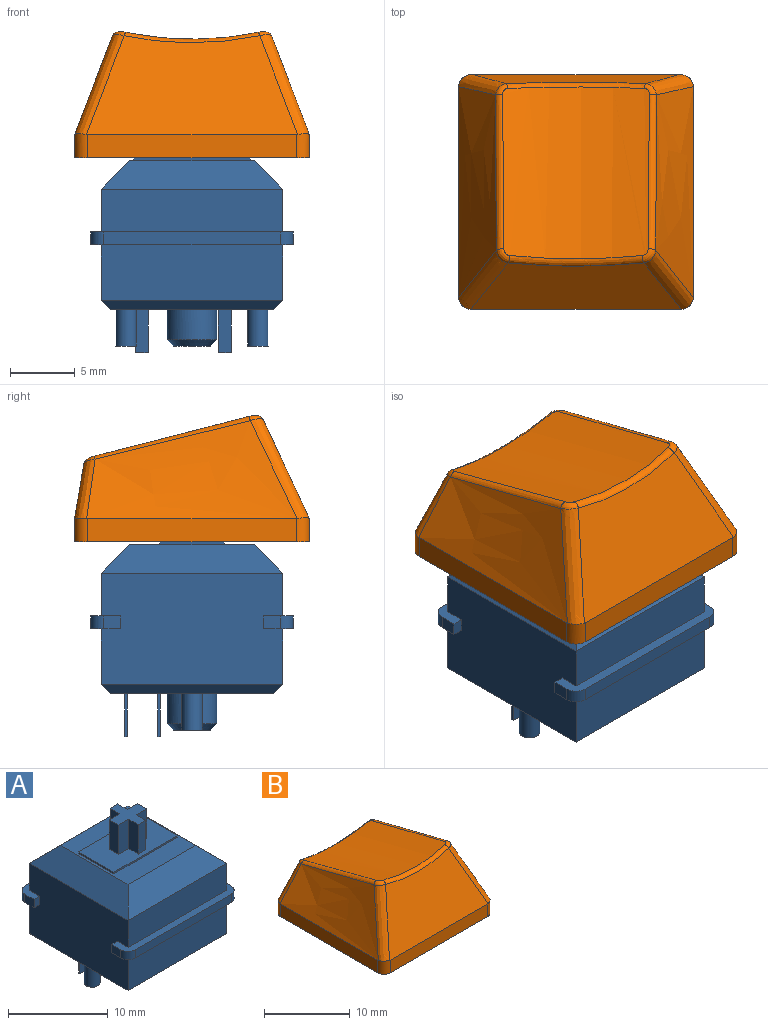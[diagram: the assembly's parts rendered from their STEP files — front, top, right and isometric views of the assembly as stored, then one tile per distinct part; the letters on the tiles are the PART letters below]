
ASSEMBLY  parts=2 mates=1
PART A: 69 faces, bbox 15.6x15.6x18.6 mm
  f0: plane 15.6x2.3mm, normal (0,0,-1), area 14.4mm2, adj f2,f3,f28,f30,f35,f60,f62,f63
  f1: plane 15.6x2.3mm, normal (0,0,-1), area 14.4mm2, adj f28,f30,f33,f34,f36,f59,f61,f64
  f2: plane 1.3x1mm, normal (1,0,0), area 1.3mm2, adj f0,f32,f62,f66
  f3: plane 1.3x1mm, normal (-1,0,0), area 1.3mm2, adj f0,f32,f63,f68
  f4: plane 15.6x2.3mm, normal (0,0,1), area 14.4mm2, adj f28,f30,f31,f33,f34,f36,f61,f64
  f5: plane 14x2.2mm, normal (-0.71,0,0.71), area 36.7mm2, adj f6,f7,f26,f30
  f6: plane 14x2.2mm, normal (0,-0.71,0.71), area 36.7mm2, adj f5,f7,f27,f31
  f7: plane 9.6x9.6mm, normal (0,0,1), area 47.2mm2, adj f5,f6,f8,f9,f10,f11,f26,f27
  f8: plane 5x0.2mm, normal (1,0,0), area 1mm2, adj f7,f9,f11,f12
  f9: plane 9x0.2mm, normal (0,1,0), area 1.8mm2, adj f7,f8,f10,f12
  f10: plane 5x0.2mm, normal (-1,0,0), area 1mm2, adj f7,f9,f11,f12
  f11: plane 9x0.2mm, normal (0,-1,0), area 1.8mm2, adj f7,f8,f10,f12
  f12: plane 9x5mm, normal (0,0,1), area 36.9mm2, adj f8,f9,f10,f11,f13,f14,f15,f16
  f13: plane 3.6x1.35mm, normal (1,0,0), area 4.9mm2, adj f12,f14,f24,f25
  f14: plane 3.6x1.08mm, normal (0,1,0), area 3.9mm2, adj f12,f13,f15,f25
  f15: plane 3.6x1.35mm, normal (-1,0,0), area 4.9mm2, adj f12,f14,f16,f25
  f16: plane 3.6x1.46mm, normal (0,1,0), area 5.3mm2, adj f12,f15,f17,f25
  f17: plane 3.6x1.3mm, normal (-1,0,0), area 4.7mm2, adj f12,f16,f18,f25
  f18: plane 3.6x1.46mm, normal (0,-1,0), area 5.3mm2, adj f12,f17,f19,f25
  f19: plane 3.6x1.35mm, normal (-1,0,0), area 4.9mm2, adj f12,f18,f20,f25
  f20: plane 3.6x1.08mm, normal (0,-1,0), area 3.9mm2, adj f12,f19,f21,f25
  f21: plane 3.6x1.35mm, normal (1,0,0), area 4.9mm2, adj f12,f20,f22,f25
  f22: plane 3.6x1.46mm, normal (0,-1,0), area 5.3mm2, adj f12,f21,f23,f25
  f23: plane 3.6x1.3mm, normal (1,0,0), area 4.7mm2, adj f12,f22,f24,f25
  f24: plane 3.6x1.46mm, normal (0,1,0), area 5.3mm2, adj f12,f13,f23,f25
  f25: plane 4x4mm, normal (0,0,1), area 8.1mm2, adj f13,f14,f15,f16,f17,f18,f19,f20
  f26: plane 14x2.2mm, normal (0,0.71,0.71), area 36.7mm2, adj f5,f7,f27,f29
  f27: plane 14x2.2mm, normal (0.71,0,0.71), area 36.7mm2, adj f6,f7,f26,f28
  f28: plane 14x8.6mm, normal (1,0,0), area 117.4mm2, adj f0,f1,f4,f27,f29,f31,f32,f55
  f29: plane 14x3.3mm, normal (0,1,0), area 46.2mm2, adj f26,f28,f30,f32
  f30: plane 14x8.6mm, normal (-1,0,0), area 117.4mm2, adj f0,f1,f4,f5,f29,f31,f32,f57
  f31: plane 14x3.3mm, normal (0,-1,0), area 46.2mm2, adj f4,f6,f28,f30
  f32: plane 15.6x2.3mm, normal (0,0,1), area 14.4mm2, adj f2,f3,f28,f29,f30,f35,f62,f63
  f33: plane 13.6x1mm, normal (0,-1,0), area 13.6mm2, adj f1,f4,f61,f64
  f34: plane 1.3x1mm, normal (1,0,0), area 1.3mm2, adj f1,f4,f61,f65
  f35: plane 13.6x1mm, normal (0,1,0), area 13.6mm2, adj f0,f32,f62,f63
  f36: plane 1.3x1mm, normal (-1,0,0), area 1.3mm2, adj f1,f4,f64,f67
  f37: plane 2.85x2.85mm, normal (0,0,-1), area 6.4mm2, adj f38
  f38: cone r=1.43mm half-angle=45deg, axis (0,0,1), area 7.4mm2, adj f37,f43
  f39: plane 1x0.2mm, normal (0,0,-1), area 0.2mm2, adj f44,f45,f46,f47
  f40: plane 1x0.2mm, normal (0,0,-1), area 0.2mm2, adj f48,f49,f50,f51
  f41: plane 1.6x1.6mm, normal (0,0,-1), area 2mm2, adj f52
  f42: plane 1.6x1.6mm, normal (0,0,-1), area 2mm2, adj f53
  f43: cylinder r=1.93mm len=3.85mm, axis (0,0,1), area 27.8mm2, adj f38,f54
  f44: plane 3.3x0.2mm, normal (-1,0,0), area 0.7mm2, adj f39,f45,f47,f54
  f45: plane 3.3x1mm, normal (0,1,0), area 3.3mm2, adj f39,f44,f46,f54
  f46: plane 3.3x0.2mm, normal (1,0,0), area 0.7mm2, adj f39,f45,f47,f54
  f47: plane 3.3x1mm, normal (0,-1,0), area 3.3mm2, adj f39,f44,f46,f54
  f48: plane 3.3x0.2mm, normal (-1,0,0), area 0.7mm2, adj f40,f49,f51,f54
  f49: plane 3.3x1mm, normal (0,1,0), area 3.3mm2, adj f40,f48,f50,f54
  f50: plane 3.3x0.2mm, normal (1,0,0), area 0.7mm2, adj f40,f49,f51,f54
  f51: plane 3.3x1mm, normal (0,-1,0), area 3.3mm2, adj f40,f48,f50,f54
  f52: cylinder r=0.8mm len=2.8mm, axis (0,0,1), area 14.1mm2, adj f41,f54
  f53: cylinder r=0.8mm len=2.8mm, axis (0,0,1), area 14.1mm2, adj f42,f54
  f54: plane 12.6x12.6mm, normal (0,0,-1), area 142.7mm2, adj f43,f44,f45,f46,f47,f48,f49,f50
  f55: plane 14x0.7mm, normal (0.71,0,-0.71), area 13.2mm2, adj f28,f54,f56,f58
  f56: plane 14x0.7mm, normal (0,0.71,-0.71), area 13.2mm2, adj f54,f55,f57,f60
  f57: plane 14x0.7mm, normal (-0.71,0,-0.71), area 13.2mm2, adj f30,f54,f56,f58
  f58: plane 14x0.7mm, normal (0,-0.71,-0.71), area 13.2mm2, adj f54,f55,f57,f59
  f59: plane 14x4.3mm, normal (0,-1,0), area 60.2mm2, adj f1,f28,f30,f58
  f60: plane 14x4.3mm, normal (0,1,0), area 60.2mm2, adj f0,f28,f30,f56
  f61: cylinder r=1mm len=1mm, axis (0,0,-1), area 1.6mm2, adj f1,f4,f33,f34
  f62: cylinder r=1mm len=1mm, axis (0,0,1), area 1.6mm2, adj f0,f2,f32,f35
  f63: cylinder r=1mm len=1mm, axis (0,0,-1), area 1.6mm2, adj f0,f3,f32,f35
  f64: cylinder r=1mm len=1mm, axis (0,0,1), area 1.6mm2, adj f1,f4,f33,f36
  f65: plane 1x0.8mm, normal (0,1,0), area 0.8mm2, adj f1,f4,f28,f34
  f66: plane 1x0.8mm, normal (0,-1,0), area 0.8mm2, adj f0,f2,f28,f32
  f67: plane 1x0.8mm, normal (0,1,0), area 0.8mm2, adj f1,f4,f30,f36
  f68: plane 1x0.8mm, normal (0,-1,0), area 0.8mm2, adj f0,f3,f30,f32
PART B: 50 faces, bbox 21.6x22.4x13.6 mm
  f0: plane 18.1x18.1mm, normal (0,0,-1), area 67.5mm2, adj f1,f2,f3,f4,f10,f12,f14,f16
  f1: plane 16.1x1.8mm, normal (1,0,0), area 29mm2, adj f0,f8,f10,f16
  f2: plane 16.1x1.8mm, normal (0,1,0), area 29mm2, adj f0,f5,f14,f15,f16,f17
  f3: plane 16.1x1.8mm, normal (-1,0,0), area 29mm2, adj f0,f6,f12,f14
  f4: plane 16.1x1.8mm, normal (0,-1,0), area 29mm2, adj f0,f7,f10,f12
  f5: plane 15.95x4.19mm, normal (0,0.99,0.17), area 51.8mm2, adj f2,f15,f17,f20
  f6: bspline ~18.1x8.19mm, area 96.8mm2, adj f3,f12,f13,f14,f15,f19
  f7: plane 16.28x7.63mm, normal (0,-0.91,0.42), area 108.3mm2, adj f4,f10,f11,f12,f13,f23
  f8: bspline ~18.1x8.19mm, area 96.8mm2, adj f1,f10,f11,f16,f17,f24
  f9: cylinder r=22.9mm len=13.05mm, axis (0,0.97,-0.25), area 150.3mm2, adj f18,f19,f20,f21,f22,f23,f24,f25
  f10: cylinder r=1mm len=1.87mm, axis (0,0,-1), area 2.9mm2, adj f0,f1,f4,f7,f8,f11
  f11: bspline ~10.14x5.57mm, area 13mm2, adj f7,f8,f10,f25
  f12: cylinder r=1mm len=1.87mm, axis (0,0,1), area 2.9mm2, adj f0,f3,f4,f6,f7,f13
  f13: bspline ~11.34x6.15mm, area 13mm2, adj f6,f7,f12,f21
  f14: cylinder r=1mm len=1.8mm, axis (0,0,-1), area 2.8mm2, adj f0,f2,f3,f6,f15
  f15: bspline ~7.36x5.16mm, area 7.5mm2, adj f2,f5,f6,f14,f18
  f16: cylinder r=1mm len=1.8mm, axis (0,0,1), area 2.8mm2, adj f0,f1,f2,f8,f17
  f17: bspline ~7.27x5.11mm, area 7.5mm2, adj f2,f5,f8,f16,f22
  f18: bspline ~1.12x0.97mm, area 0.6mm2, adj f9,f15,f19,f20
  f19: bspline ~18.33x4.95mm, area 8.5mm2, adj f6,f9,f18,f21
  f20: bspline ~10.76x1.07mm, area 6.2mm2, adj f5,f9,f18,f22
  f21: bspline ~1.23x1.17mm, area 0.8mm2, adj f9,f13,f19,f23
  f22: bspline ~1.1x0.93mm, area 0.6mm2, adj f9,f17,f20,f24
  f23: bspline ~10.45x0.83mm, area 7.2mm2, adj f7,f9,f21,f25
  f24: bspline ~18.29x4.94mm, area 8.5mm2, adj f8,f9,f22,f25
  f25: bspline ~1.33x1.08mm, area 0.8mm2, adj f9,f11,f23,f24
  f26: plane 16.18x1.7mm, normal (-1,0,0), area 25.3mm2, adj f0,f27,f29,f32,f33
  f27: plane 16.1x1.72mm, normal (0,-1,0), area 27.6mm2, adj f0,f26,f28,f30,f31,f33
  f28: plane 16.18x1.7mm, normal (1,0,0), area 25.3mm2, adj f0,f27,f29,f31,f32
  f29: plane 16.1x1.58mm, normal (0,1,0), area 25.4mm2, adj f0,f26,f28,f32
  f30: plane 16.43x4.41mm, normal (0,-0.99,-0.17), area 46.9mm2, adj f27,f31,f33,f34
  f31: offset ~20.1x10.19mm, area 87.9mm2, adj f27,f28,f30,f32,f34
  f32: plane 16.33x7.29mm, normal (0,0.91,-0.42), area 100.3mm2, adj f26,f28,f29,f31,f33,f34
  f33: offset ~20.1x10.19mm, area 87.9mm2, adj f26,f27,f30,f32,f34
  f34: cylinder r=23.9mm len=12.31mm, axis (0,0.97,-0.25), area 113.6mm2, adj f30,f31,f32,f33,f46
  f35: plane 6.62x1.35mm, normal (-1,0,0), area 8.7mm2, adj f36,f44,f45,f49
  f36: plane 6.7x1.51mm, normal (0,-1,0), area 10mm2, adj f35,f37,f45,f49
  f37: plane 7.03x1.3mm, normal (-1,0,0), area 8.9mm2, adj f36,f38,f45,f49
  f38: plane 7.04x1.51mm, normal (0,1,0), area 10.5mm2, adj f37,f39,f45,f49
  f39: plane 7.3x1.35mm, normal (-1,0,0), area 9.6mm2, adj f38,f40,f45,f49
  f40: plane 7.31x1mm, normal (0,1,0), area 7.3mm2, adj f39,f41,f45,f49
  f41: plane 7.3x1.35mm, normal (1,0,0), area 9.6mm2, adj f40,f42,f45,f49
  f42: plane 7.04x1.51mm, normal (0,1,0), area 10.5mm2, adj f41,f43,f45,f49
  f43: plane 7.03x1.3mm, normal (1,0,0), area 8.9mm2, adj f42,f45,f47,f49
  f44: plane 6.27x1mm, normal (0,-1,0), area 6.3mm2, adj f35,f45,f48,f49
  f45: plane 5.5x5.5mm, normal (0,0,-1), area 15.9mm2, adj f35,f36,f37,f38,f39,f40,f41,f42
  f46: cylinder r=2.75mm len=6.94mm, axis (0,0,-1), area 120mm2, adj f34,f45
  f47: plane 6.7x1.51mm, normal (0,-1,0), area 10mm2, adj f43,f45,f48,f49
  f48: plane 6.62x1.35mm, normal (1,0,0), area 8.7mm2, adj f44,f45,f47,f49
  f49: cylinder r=23.9mm len=4.02mm, axis (0,0.97,-0.25), area 8.2mm2, adj f35,f36,f37,f38,f39,f40,f41,f42
PLACE A at identity fixed
PLACE B t=(0,0,11.7)mm
MATE fastened A.f38 <-> B.f46  axis (0,0,1) through (0,0,11.7)mm
